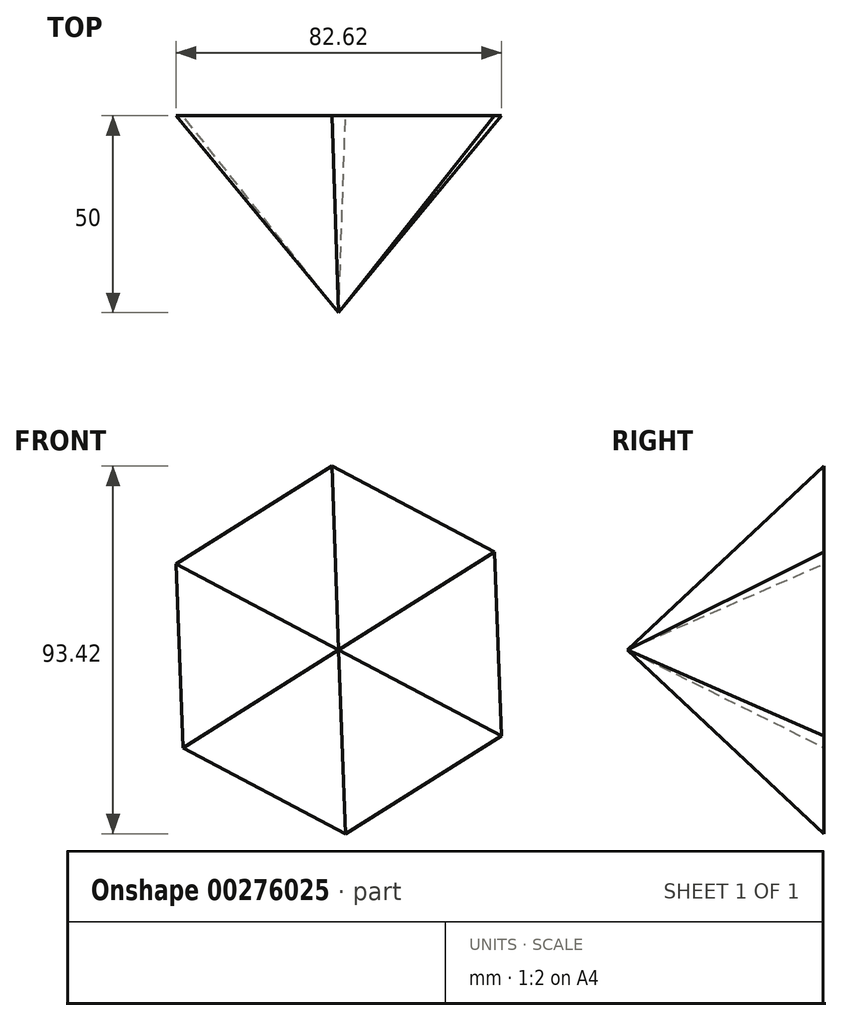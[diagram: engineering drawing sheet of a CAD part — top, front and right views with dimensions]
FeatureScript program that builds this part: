
annotation { "Feature Type Name" : "Feature", "Feature Type Description" : "" }
export const myFeature = defineFeature(function(context is Context, id is Id, definition is map)
    precondition{}
    {
        {
            var Q0;
            Q0=qCreatedBy(makeId("Front.planeOp"),FACE);
            var sketch = newSketch(context, id + "F0", { "sketchPlane" : qUnion([Q0])});
            skCircle(sketch, "E0.cCircle", {"center": v(0, 0) * mm, "radius": 40.48 * mm, "construction": true});
            skLineSegment(sketch, "E0.0", {"start": v(-41.3, 21.86) * mm, "end": v(-1.72, 46.7) * mm});
            skLineSegment(sketch, "E0.1", {"start": v(-1.72, 46.7) * mm, "end": v(39.59, 24.84) * mm});
            skLineSegment(sketch, "E0.2", {"start": v(39.59, 24.84) * mm, "end": v(41.3, -21.86) * mm});
            skLineSegment(sketch, "E0.3", {"start": v(41.3, -21.86) * mm, "end": v(1.72, -46.7) * mm});
            skLineSegment(sketch, "E0.4", {"start": v(1.72, -46.7) * mm, "end": v(-39.59, -24.84) * mm});
            skLineSegment(sketch, "E0.5", {"start": v(-39.59, -24.84) * mm, "end": v(-41.3, 21.86) * mm});
            skPoint(sketch, "E0.0.midPoint", {"position": v(-21.52, 34.28) * mm});
            skSolve(sketch);
        }
        {
            var Q0;
            Q0=qCreatedBy(makeId("Front.planeOp"),FACE);
            cPlane(context, id + "F1", {"entities" : qUnion([Q0]), "cplaneType" : CPlaneType.OFFSET, "offset" : 50 * mm, "width" : 150 * mm, "height" : 150 * mm});
        }
        {
            var Q0;
            Q0=qCreatedBy(id+"F1.planeOp",FACE);
            var sketch = newSketch(context, id + "F2", { "sketchPlane" : qUnion([Q0])});
            skPoint(sketch, "E1", {"position": v(0, 0) * mm});
            skSolve(sketch);
        }
        {
            var Q0;
            Q0=sQuery(id+"F2.wireOp",VERTEX,"E1");
            var Q1;
            Q1=makeQuery(id+"F0.imprint","IMPRINT",FACE,{"disambiguationData":[TD([[makeQuery(id+"F0.imprint","IMPRINT",EDGE,{"derivedFrom":sQuery(id+"F0.wireOp",EDGE,"E0.0")}),-1.0]])]});
            loft(context, id + "F3", {"sheetProfilesArray" : [{ "sheetProfileEntities" : qUnion([Q0]) }, { "sheetProfileEntities" : qUnion([Q1]) }]});
        }
    });
